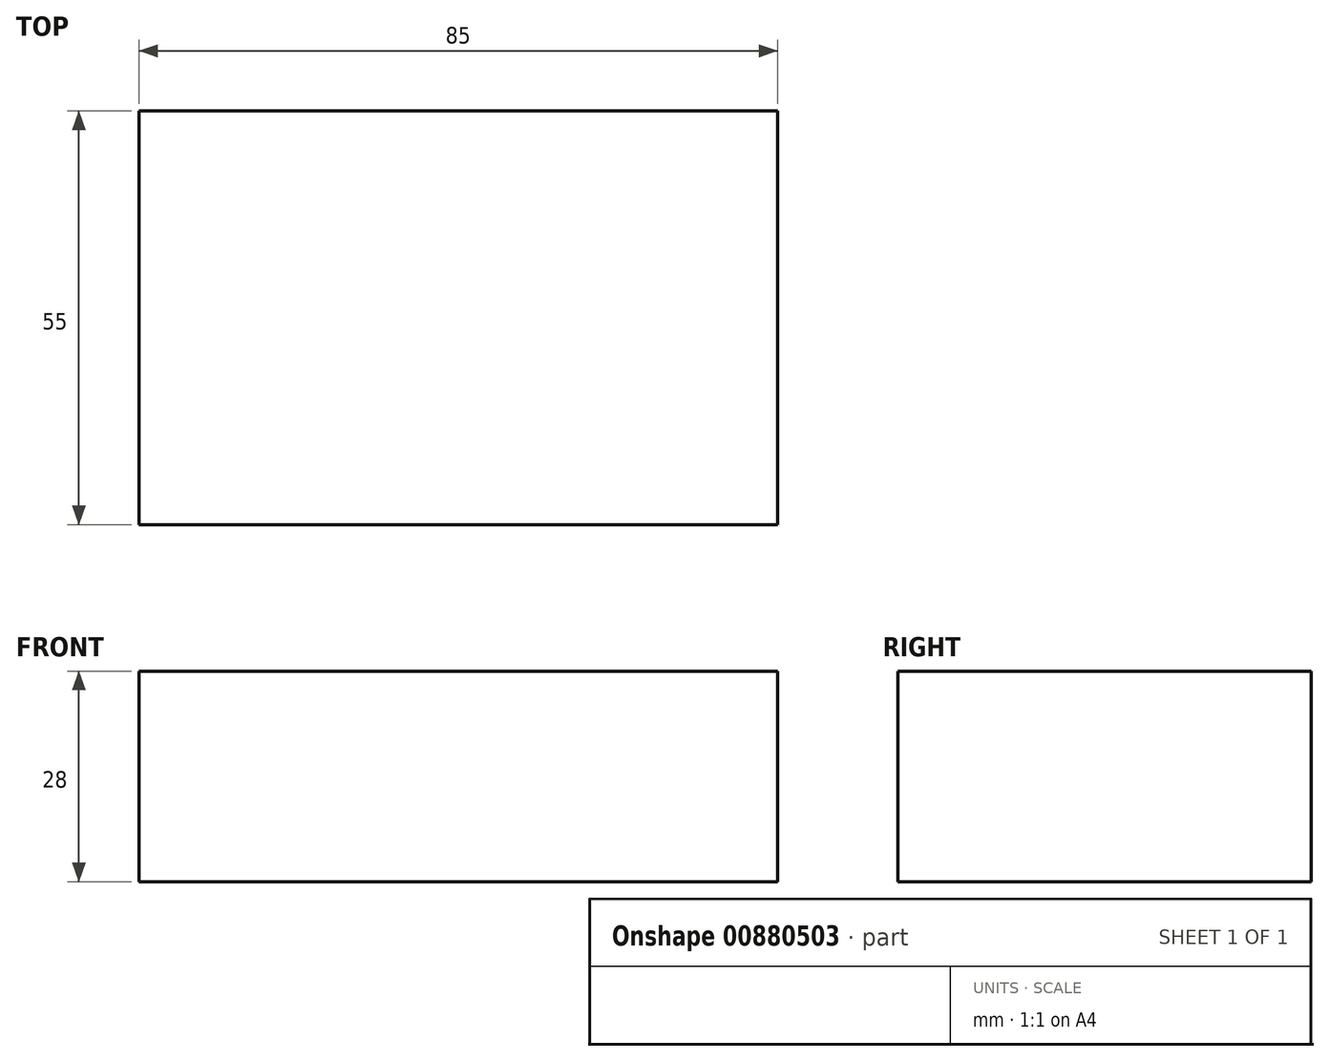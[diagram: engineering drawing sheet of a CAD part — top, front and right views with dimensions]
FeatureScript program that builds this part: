
annotation { "Feature Type Name" : "Feature", "Feature Type Description" : "" }
export const myFeature = defineFeature(function(context is Context, id is Id, definition is map)
    precondition{}
    {
        {
            var Q0;
            Q0=qCreatedBy(makeId("Top.planeOp"),FACE);
            var sketch = newSketch(context, id + "F0", { "sketchPlane" : qUnion([Q0])});
            skLineSegment(sketch, "E0.bottom", {"start": v(-42.5, 27.5) * mm, "end": v(42.5, 27.5) * mm});
            skLineSegment(sketch, "E0.top", {"start": v(-42.5, -27.5) * mm, "end": v(42.5, -27.5) * mm});
            skLineSegment(sketch, "E0.left", {"start": v(-42.5, 27.5) * mm, "end": v(-42.5, -27.5) * mm});
            skLineSegment(sketch, "E0.right", {"start": v(42.5, 27.5) * mm, "end": v(42.5, -27.5) * mm});
            skSolve(sketch);
        }
        {
            var Q0;
            Q0=makeQuery(id+"F0.imprint","IMPRINT",FACE,{"disambiguationData":[TD([[makeQuery(id+"F0.imprint","IMPRINT",EDGE,{"derivedFrom":sQuery(id+"F0.wireOp",EDGE,"E0.bottom")}),-1.0]])]});
            extrude(context, id + "F1", {"entities" : qUnion([Q0]), "depth" : 28 * mm, "offsetDistance" : 25 * mm});
        }
    });
